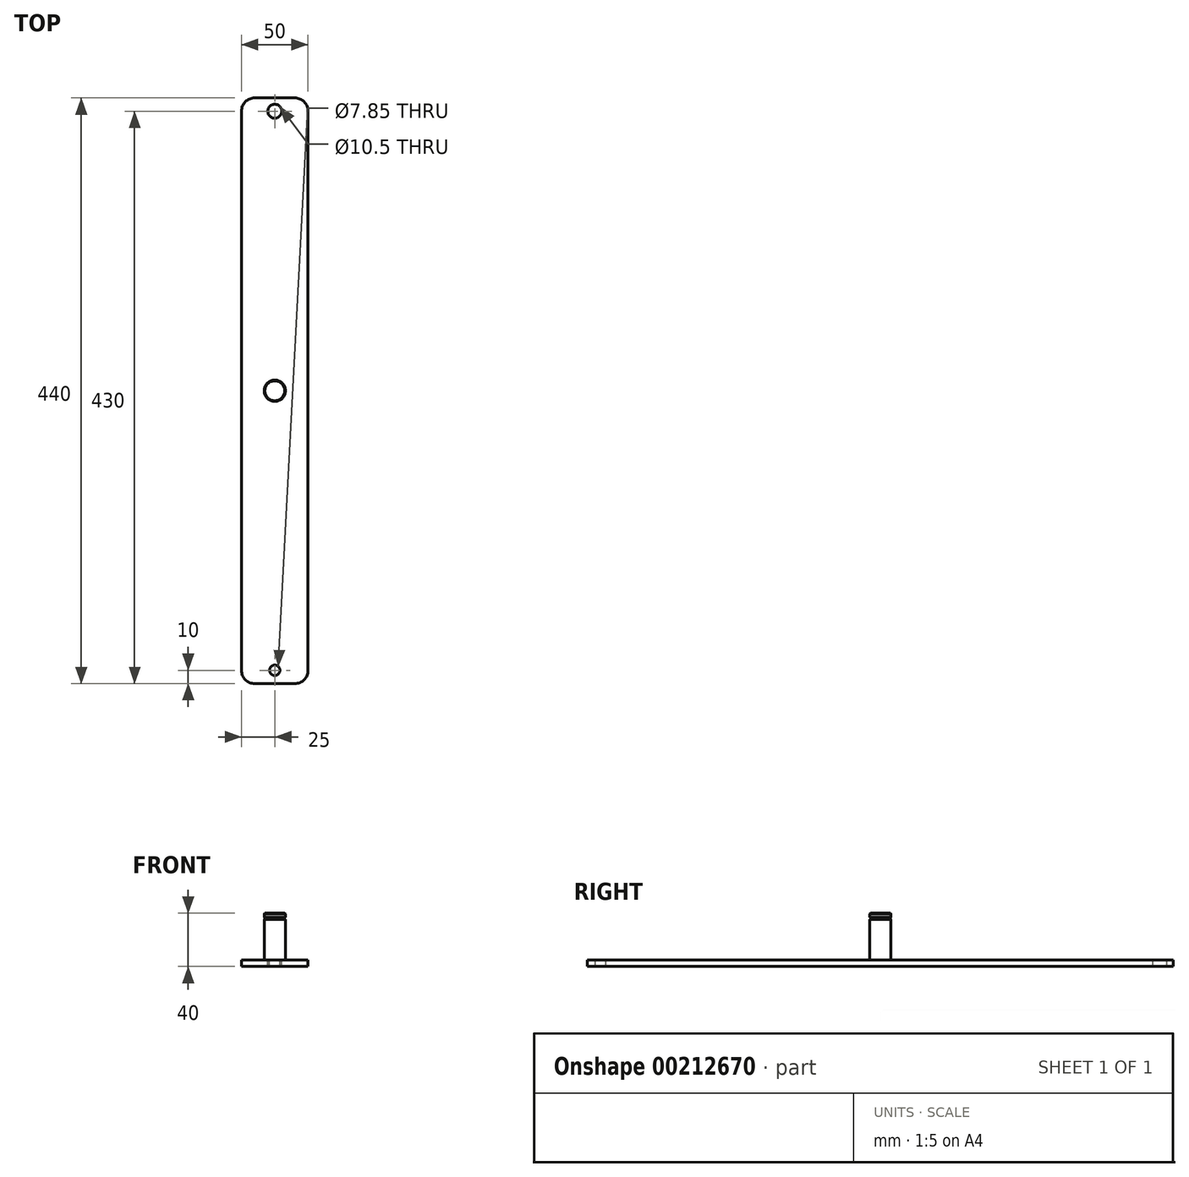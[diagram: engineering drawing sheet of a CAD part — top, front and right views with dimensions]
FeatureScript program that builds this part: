
annotation { "Feature Type Name" : "Feature", "Feature Type Description" : "" }
export const myFeature = defineFeature(function(context is Context, id is Id, definition is map)
    precondition{}
    {
        {
            var Q0;
            Q0=qCreatedBy(makeId("Front.planeOp"),FACE);
            var sketch = newSketch(context, id + "F0", { "sketchPlane" : qUnion([Q0])});
            skLineSegment(sketch, "E0.bottom", {"start": v(-25, 2.5) * mm, "end": v(25, 2.5) * mm});
            skLineSegment(sketch, "E0.top", {"start": v(-25, -2.5) * mm, "end": v(25, -2.5) * mm});
            skLineSegment(sketch, "E0.left", {"start": v(-25, 2.5) * mm, "end": v(-25, -2.5) * mm});
            skLineSegment(sketch, "E0.right", {"start": v(25, 2.5) * mm, "end": v(25, -2.5) * mm});
            skSolve(sketch);
        }
        {
            var Q0;
            Q0 = qSketchRegion(id + "F0", true);
            extrude(context, id + "F1", {"entities" : qUnion([Q0]), "depth" : 440 * mm});
        }
        {
            var Q0;
            Q0=makeQuery(id+"F1.opExtrude","SWEPT_FACE",FACE,{"disambiguationData":[OSD([sQuery(id+"F0.wireOp",EDGE,"E0.bottom")])]});
            var sketch = newSketch(context, id + "F2", { "sketchPlane" : qUnion([Q0])});
            skCircle(sketch, "E1", {"center": v(0, -10) * mm, "radius": 5.25 * mm});
            skCircle(sketch, "E2", {"center": v(0, -430) * mm, "radius": 3.93 * mm});
            skSolve(sketch);
        }
        {
            var Q0;
            Q0 = qSketchRegion(id + "F2", true);
            extrude(context, id + "F3", {"entities" : qUnion([Q0]), "operationType" : NewBodyOperationType.REMOVE, "endBound" : BoundingType.THROUGH_ALL, "oppositeDirection" : true, "depth" : 25 * mm});
        }
        {
            var Q0;
            Q0=makeQuery(id+"F1.opExtrude","SWEPT_FACE",FACE,{"disambiguationData":[OSD([sQuery(id+"F0.wireOp",EDGE,"E0.bottom")])]});
            var sketch = newSketch(context, id + "F4", { "sketchPlane" : qUnion([Q0])});
            skCircle(sketch, "E3", {"center": v(0, -220) * mm, "radius": 8 * mm});
            skSolve(sketch);
        }
        {
            var Q0;
            Q0 = qSketchRegion(id + "F4", true);
            extrude(context, id + "F5", {"entities" : qUnion([Q0]), "operationType" : NewBodyOperationType.ADD, "depth" : 35 * mm});
        }
        {
            var Q0;
            Q0=makeQuery(id+"F1.opExtrude","CAP_EDGE",EDGE,{"disambiguationData":[OSD([sQuery(id+"F0.wireOp",EDGE,"E0.left")])],"isStart":false});
            var Q1;
            Q1=makeQuery(id+"F1.opExtrude","CAP_EDGE",EDGE,{"disambiguationData":[OSD([sQuery(id+"F0.wireOp",EDGE,"E0.right")])],"isStart":false});
            var Q2;
            Q2=makeQuery(id+"F1.opExtrude","CAP_EDGE",EDGE,{"disambiguationData":[OSD([sQuery(id+"F0.wireOp",EDGE,"E0.right")])],"isStart":true});
            var Q3;
            Q3=makeQuery(id+"F1.opExtrude","CAP_EDGE",EDGE,{"disambiguationData":[OSD([sQuery(id+"F0.wireOp",EDGE,"E0.left")])],"isStart":true});
            fillet(context, id + "F6", {"entities" : qUnion([Q0, Q1, Q2, Q3]), "radius" : 10 * mm, "tangentPropagation" : true, "allowEdgeOverflow" : false});
        }
        {
            var Q0;
            Q0=makeQuery(id+"F5.opExtrude","CAP_FACE",FACE,{"disambiguationData":[OSD([sQuery(id+"F4.wireOp",EDGE,"E3")])],"isStart":false});
            cPlane(context, id + "F7", {"entities" : qUnion([Q0]), "cplaneType" : CPlaneType.OFFSET, "offset" : 3 * mm, "oppositeDirection" : true, "width" : 150 * mm, "height" : 150 * mm});
        }
        {
            var Q0;
            Q0=qCreatedBy(id+"F7.planeOp",FACE);
            var sketch = newSketch(context, id + "F8", { "sketchPlane" : qUnion([Q0])});
            skCircle(sketch, "E4", {"center": v(0, -220) * mm, "radius": 7.5 * mm});
            skCircle(sketch, "E5", {"center": v(0, -220) * mm, "radius": 8 * mm});
            skSolve(sketch);
        }
        {
            var Q0;
            Q0 = qSketchRegion(id + "F8", true);
            extrude(context, id + "F9", {"entities" : qUnion([Q0]), "operationType" : NewBodyOperationType.REMOVE, "oppositeDirection" : true, "depth" : 1.5 * mm});
        }
        {
            var Q0;
            Q0=makeQuery(id+"F5.opExtrude","CAP_EDGE",EDGE,{"disambiguationData":[OSD([sQuery(id+"F4.wireOp",EDGE,"E3")])],"isStart":false});
            chamfer(context, id + "F10", {"entities" : qUnion([Q0]), "width" : .5 * mm, "tangentPropagation" : true});
        }
    });
